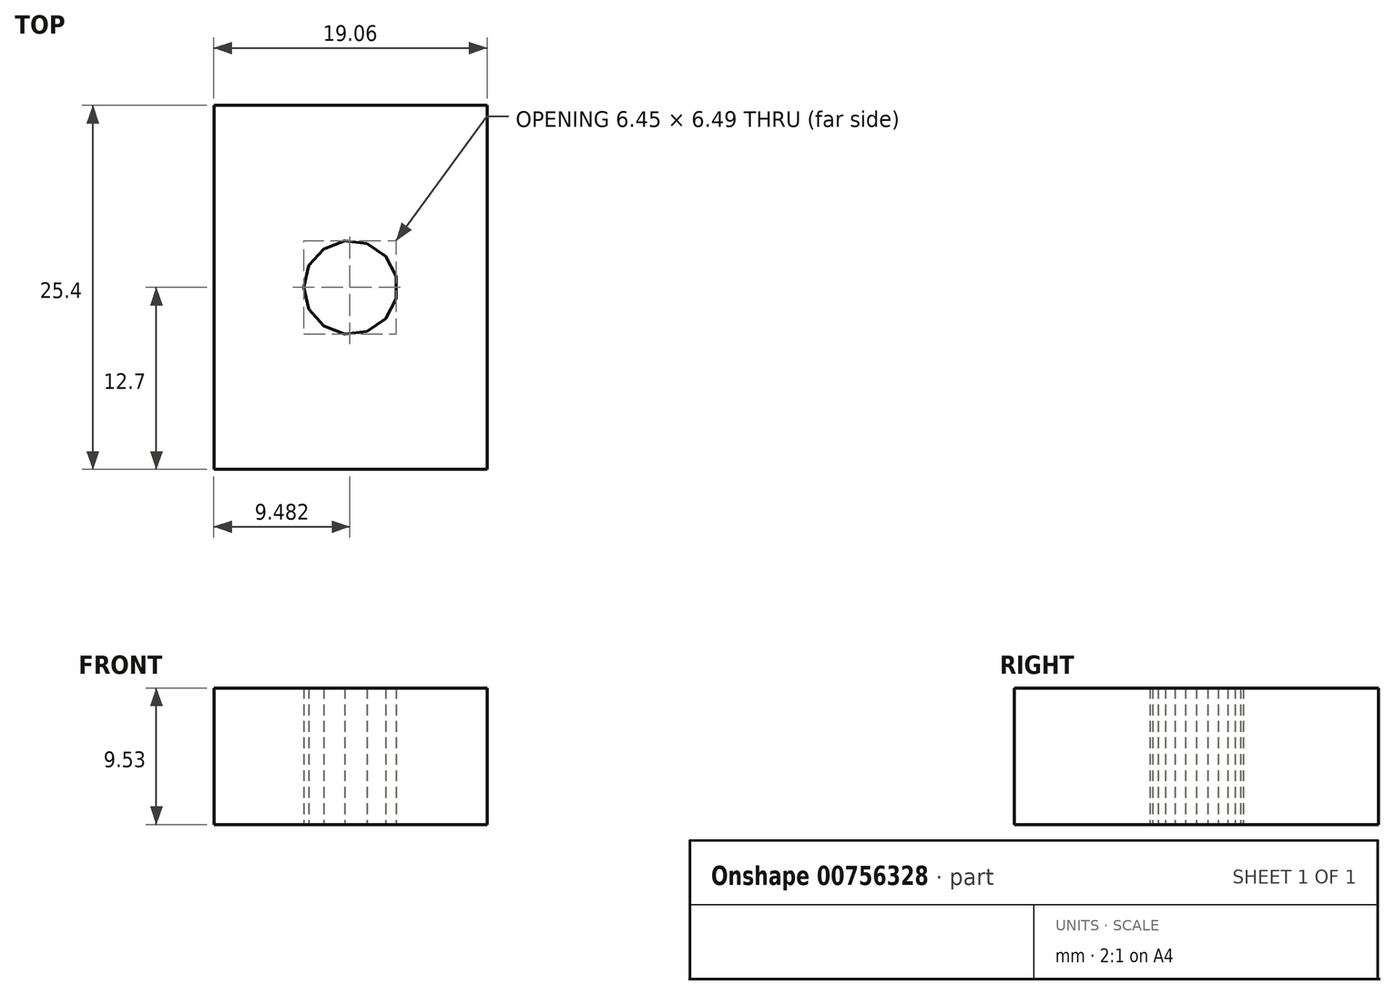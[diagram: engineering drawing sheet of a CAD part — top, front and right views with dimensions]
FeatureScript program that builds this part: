
annotation { "Feature Type Name" : "Feature", "Feature Type Description" : "" }
export const myFeature = defineFeature(function(context is Context, id is Id, definition is map)
    precondition{}
    {
        {
            var Q0;
            Q0=qCreatedBy(makeId("Top.planeOp"),FACE);
            var sketch = newSketch(context, id + "F0", { "sketchPlane" : qUnion([Q0])});
            skLineSegment(sketch, "E0.bottom", {"start": v(9.52, 12.7) * mm, "end": v(-9.53, 12.7) * mm});
            skLineSegment(sketch, "E0.top", {"start": v(9.52, -12.7) * mm, "end": v(-9.52, -12.7) * mm});
            skLineSegment(sketch, "E0.left", {"start": v(9.52, 12.7) * mm, "end": v(9.53, -12.7) * mm});
            skLineSegment(sketch, "E0.right", {"start": v(-9.53, 12.7) * mm, "end": v(-9.52, -12.7) * mm});
            skPoint(sketch, "E0.middle", {"position": v(0, 0) * mm});
            skCircle(sketch, "E1.cCircle", {"center": v(0, 0) * mm, "radius": 3.18 * mm, "construction": true});
            skLineSegment(sketch, "E1.0", {"start": v(3.18, 0.78) * mm, "end": v(3.18, -0.78) * mm});
            skLineSegment(sketch, "E1.1", {"start": v(3.17, -0.78) * mm, "end": v(2.45, -2.17) * mm});
            skLineSegment(sketch, "E1.2", {"start": v(2.45, -2.17) * mm, "end": v(1.16, -3.06) * mm});
            skLineSegment(sketch, "E1.3", {"start": v(1.16, -3.06) * mm, "end": v(-0.4, -3.25) * mm});
            skLineSegment(sketch, "E1.4", {"start": v(-0.4, -3.25) * mm, "end": v(-1.86, -2.7) * mm});
            skLineSegment(sketch, "E1.5", {"start": v(-1.86, -2.7) * mm, "end": v(-2.9, -1.52) * mm});
            skLineSegment(sketch, "E1.6", {"start": v(-2.9, -1.52) * mm, "end": v(-3.27, 0) * mm});
            skLineSegment(sketch, "E1.7", {"start": v(-3.27, 0) * mm, "end": v(-2.9, 1.52) * mm});
            skLineSegment(sketch, "E1.8", {"start": v(-2.9, 1.52) * mm, "end": v(-1.86, 2.7) * mm});
            skLineSegment(sketch, "E1.9", {"start": v(-1.86, 2.7) * mm, "end": v(-0.4, 3.25) * mm});
            skLineSegment(sketch, "E1.10", {"start": v(-0.4, 3.25) * mm, "end": v(1.16, 3.06) * mm});
            skLineSegment(sketch, "E1.11", {"start": v(1.16, 3.06) * mm, "end": v(2.45, 2.17) * mm});
            skLineSegment(sketch, "E1.12", {"start": v(2.45, 2.17) * mm, "end": v(3.18, 0.78) * mm});
            skPoint(sketch, "E1.0.midPoint", {"position": v(3.18, 0) * mm});
            skSolve(sketch);
        }
        {
            var Q0;
            Q0=makeQuery(id+"F0.imprint","IMPRINT",FACE,{"disambiguationData":[TD([[makeQuery(id+"F0.imprint","IMPRINT",EDGE,{"derivedFrom":sQuery(id+"F0.wireOp",EDGE,"E0.bottom")}),1.0]])]});
            extrude(context, id + "F1", {"entities" : qUnion([Q0]), "depth" : 9.52 * mm, "offsetDistance" : 25.4 * mm});
        }
    });
